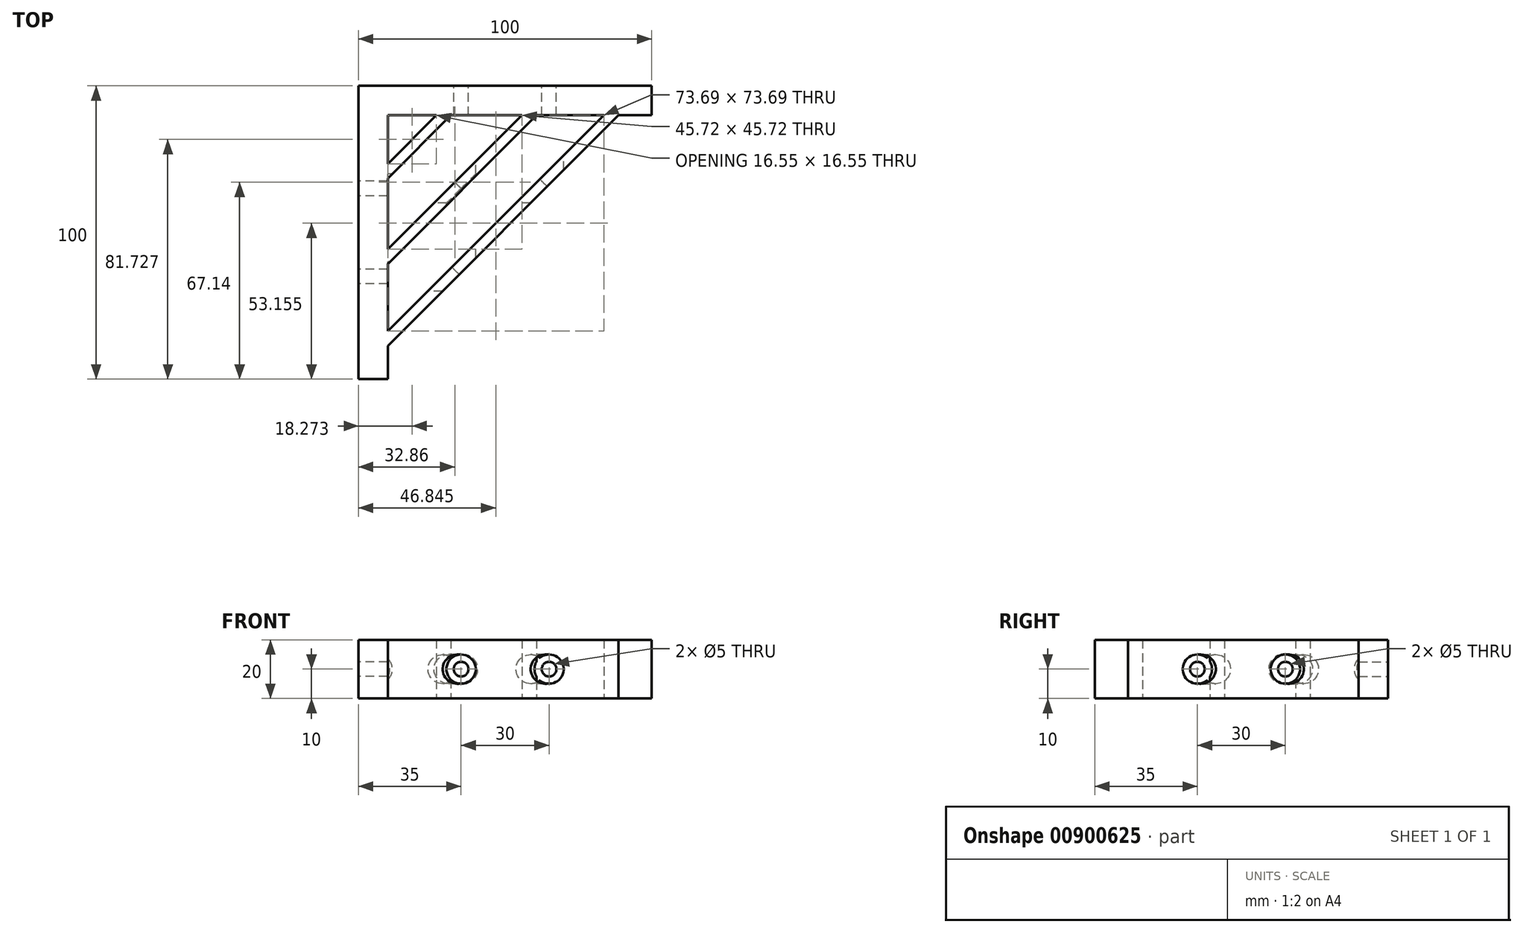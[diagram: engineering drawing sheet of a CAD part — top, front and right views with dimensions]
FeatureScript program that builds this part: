
annotation { "Feature Type Name" : "Feature", "Feature Type Description" : "" }
export const myFeature = defineFeature(function(context is Context, id is Id, definition is map)
    precondition{}
    {
        {
            var Q0;
            Q0=qCreatedBy(makeId("Top.planeOp"),FACE);
            var sketch = newSketch(context, id + "F0", { "sketchPlane" : qUnion([Q0])});
            skLineSegment(sketch, "E0.bottom", {"start": v(-55.72, 55.72) * mm, "end": v(-45.72, 55.72) * mm});
            skLineSegment(sketch, "E0.top", {"start": v(-55.72, -44.28) * mm, "end": v(-45.72, -44.28) * mm});
            skLineSegment(sketch, "E0.left", {"start": v(-55.72, 55.72) * mm, "end": v(-55.72, -44.28) * mm});
            skLineSegment(sketch, "E0.right", {"start": v(-45.72, 55.72) * mm, "end": v(-45.72, -44.28) * mm});
            skLineSegment(sketch, "E1.bottom", {"start": v(-55.72, 55.72) * mm, "end": v(44.28, 55.72) * mm});
            skLineSegment(sketch, "E1.top", {"start": v(-55.72, 45.72) * mm, "end": v(44.28, 45.72) * mm});
            skLineSegment(sketch, "E1.left", {"start": v(-55.72, 55.72) * mm, "end": v(-55.72, 45.72) * mm});
            skLineSegment(sketch, "E1.right", {"start": v(44.28, 55.72) * mm, "end": v(44.28, 45.72) * mm});
            skLineSegment(sketch, "E2", {"start": v(-55.72, 55.72) * mm, "end": v(0, 0) * mm, "construction": true});
            skLineSegment(sketch, "E3", {"start": v(0, 0) * mm, "end": v(47.24, -47.24) * mm, "construction": true});
            skLineSegment(sketch, "E4", {"start": v(-45.72, 29.17) * mm, "end": v(-29.17, 45.72) * mm});
            skLineSegment(sketch, "E5", {"start": v(-29.17, 45.72) * mm, "end": v(-24.17, 45.72) * mm});
            skLineSegment(sketch, "E6", {"start": v(-24.17, 45.72) * mm, "end": v(-45.72, 24.17) * mm});
            skLineSegment(sketch, "E7", {"start": v(-45.72, 0) * mm, "end": v(0, 45.72) * mm});
            skLineSegment(sketch, "E8", {"start": v(0, 45.72) * mm, "end": v(5, 45.72) * mm});
            skLineSegment(sketch, "E9", {"start": v(5, 45.72) * mm, "end": v(-45.72, -5) * mm});
            skLineSegment(sketch, "E10", {"start": v(-45.72, -5) * mm, "end": v(-45.72, 0) * mm});
            skLineSegment(sketch, "E11", {"start": v(-45.72, -27.97) * mm, "end": v(27.97, 45.72) * mm});
            skLineSegment(sketch, "E12", {"start": v(27.97, 45.72) * mm, "end": v(32.97, 45.72) * mm});
            skLineSegment(sketch, "E13", {"start": v(32.97, 45.72) * mm, "end": v(-45.72, -32.97) * mm});
            skLineSegment(sketch, "E14", {"start": v(-45.72, -32.97) * mm, "end": v(-45.72, -27.97) * mm});
            skSolve(sketch);
        }
        {
            var Q0;
            {var subQ6=sQuery(id+"F0.wireOp",EDGE,"E0.top");Q0=makeQuery(id+"F0.imprint","IMPRINT",FACE,{"disambiguationData":[TD([[makeQuery(id+"F0.imprint","IMPRINT",EDGE,{"derivedFrom":subQ6}),1.0]])]});}
            var Q1;
            {var subQ0=sQuery(id+"F0.wireOp",EDGE,"E0.bottom");Q1=makeQuery(id+"F0.imprint","IMPRINT",FACE,{"disambiguationData":[TD([[makeQuery(id+"F0.imprint","IMPRINT",EDGE,{"derivedFrom":subQ0}),-1.0]])]});}
            var Q2;
            {var subQ3=sQuery(id+"F0.wireOp",EDGE,"E1.bottom");Q2=makeQuery(id+"F0.imprint","IMPRINT",FACE,{"disambiguationData":[TD([[makeQuery(id+"F0.imprint","IMPRINT",EDGE,{"derivedFrom":subQ3}),-1.0]])]});}
            var Q3;
            {var subQ2=sQuery(id+"F0.wireOp",EDGE,"E4");Q3=makeQuery(id+"F0.imprint","IMPRINT",FACE,{"disambiguationData":[TD([[makeQuery(id+"F0.imprint","IMPRINT",EDGE,{"derivedFrom":subQ2}),-1.0]])]});}
            var Q4;
            {var subQ0=sQuery(id+"F0.wireOp",EDGE,"E7");Q4=makeQuery(id+"F0.imprint","IMPRINT",FACE,{"disambiguationData":[TD([[makeQuery(id+"F0.imprint","IMPRINT",EDGE,{"derivedFrom":subQ0}),-1.0]])]});}
            var Q5;
            {var subQ0=sQuery(id+"F0.wireOp",EDGE,"E11");Q5=makeQuery(id+"F0.imprint","IMPRINT",FACE,{"disambiguationData":[TD([[makeQuery(id+"F0.imprint","IMPRINT",EDGE,{"derivedFrom":subQ0}),-1.0]])]});}
            extrude(context, id + "F1", {"entities" : qUnion([Q0, Q1, Q2, Q3, Q4, Q5]), "depth" : 20 * mm, "offsetDistance" : 25 * mm});
        }
        {
            var Q0;
            Q0=makeQuery(id+"F1.opExtrude","SWEPT_FACE",FACE,{"disambiguationData":[OSD([sQuery(id+"F0.wireOp",EDGE,"E0.left")])]});
            var sketch = newSketch(context, id + "F2", { "sketchPlane" : qUnion([Q0])});
            skLineSegment(sketch, "E15", {"start": v(-55.72, 10) * mm, "end": v(44.28, 10) * mm, "construction": true});
            skLineSegment(sketch, "E16", {"start": v(-55.72, 10) * mm, "end": v(-20.72, 10) * mm, "construction": true});
            skLineSegment(sketch, "E17", {"start": v(44.28, 10) * mm, "end": v(9.28, 10) * mm, "construction": true});
            skCircle(sketch, "E18", {"center": v(-20.72, 10) * mm, "radius": 2.5 * mm});
            skCircle(sketch, "E19", {"center": v(9.28, 10) * mm, "radius": 2.5 * mm});
            skCircle(sketch, "E20", {"center": v(9.28, 10) * mm, "radius": 5 * mm});
            skCircle(sketch, "E21", {"center": v(-20.72, 10) * mm, "radius": 5 * mm});
            skSolve(sketch);
        }
        {
            var Q0;
            Q0=makeQuery(id+"F2.imprint","IMPRINT",FACE,{"disambiguationData":[TD([[makeQuery(id+"F2.imprint","IMPRINT",EDGE,{"derivedFrom":sQuery(id+"F2.wireOp",EDGE,"E19")}),1.0]])]});
            var Q1;
            Q1=makeQuery(id+"F2.imprint","IMPRINT",FACE,{"disambiguationData":[TD([[makeQuery(id+"F2.imprint","IMPRINT",EDGE,{"derivedFrom":sQuery(id+"F2.wireOp",EDGE,"E19")}),-1.0]])]});
            var Q2;
            Q2=makeQuery(id+"F2.imprint","IMPRINT",FACE,{"disambiguationData":[TD([[makeQuery(id+"F2.imprint","IMPRINT",EDGE,{"derivedFrom":sQuery(id+"F2.wireOp",EDGE,"E18")}),-1.0]])]});
            var Q3;
            Q3=makeQuery(id+"F2.imprint","IMPRINT",FACE,{"disambiguationData":[TD([[makeQuery(id+"F2.imprint","IMPRINT",EDGE,{"derivedFrom":sQuery(id+"F2.wireOp",EDGE,"E18")}),1.0]])]});
            extrude(context, id + "F3", {"entities" : qUnion([Q0, Q1, Q2, Q3]), "operationType" : NewBodyOperationType.REMOVE, "oppositeDirection" : true, "depth" : 86.8 * mm, "offsetDistance" : 25 * mm});
        }
        {
            var Q0;
            Q0=makeQuery(id+"F2.imprint","IMPRINT",FACE,{"disambiguationData":[TD([[makeQuery(id+"F2.imprint","IMPRINT",EDGE,{"derivedFrom":sQuery(id+"F2.wireOp",EDGE,"E18")}),-1.0]])]});
            var Q1;
            Q1=makeQuery(id+"F2.imprint","IMPRINT",FACE,{"disambiguationData":[TD([[makeQuery(id+"F2.imprint","IMPRINT",EDGE,{"derivedFrom":sQuery(id+"F2.wireOp",EDGE,"E19")}),-1.0]])]});
            extrude(context, id + "F4", {"entities" : qUnion([Q0, Q1]), "operationType" : NewBodyOperationType.ADD, "oppositeDirection" : true, "depth" : 10 * mm, "offsetDistance" : 25 * mm});
        }
        {
            var Q0;
            Q0=makeQuery(id+"F1.opExtrude","SWEPT_FACE",FACE,{"disambiguationData":[OSD([sQuery(id+"F0.wireOp",EDGE,"E0.bottom"),sQuery(id+"F0.wireOp",EDGE,"E1.bottom")])]});
            var sketch = newSketch(context, id + "F5", { "sketchPlane" : qUnion([Q0])});
            skLineSegment(sketch, "E22", {"start": v(55.72, 10) * mm, "end": v(20.72, 10) * mm, "construction": true});
            skLineSegment(sketch, "E23", {"start": v(-44.28, 10) * mm, "end": v(-9.28, 10) * mm, "construction": true});
            skCircle(sketch, "E24", {"center": v(20.72, 10) * mm, "radius": 5 * mm});
            skCircle(sketch, "E25", {"center": v(20.72, 10) * mm, "radius": 2.5 * mm});
            skCircle(sketch, "E26", {"center": v(-9.28, 10) * mm, "radius": 5 * mm});
            skCircle(sketch, "E27", {"center": v(-9.28, 10) * mm, "radius": 2.5 * mm});
            skSolve(sketch);
        }
        {
            var Q0;
            Q0=makeQuery(id+"F5.imprint","IMPRINT",FACE,{"disambiguationData":[TD([[makeQuery(id+"F5.imprint","IMPRINT",EDGE,{"derivedFrom":sQuery(id+"F5.wireOp",EDGE,"E25")}),1.0]])]});
            var Q1;
            Q1=makeQuery(id+"F5.imprint","IMPRINT",FACE,{"disambiguationData":[TD([[makeQuery(id+"F5.imprint","IMPRINT",EDGE,{"derivedFrom":sQuery(id+"F5.wireOp",EDGE,"E24")}),1.0]])]});
            var Q2;
            Q2=makeQuery(id+"F5.imprint","IMPRINT",FACE,{"disambiguationData":[TD([[makeQuery(id+"F5.imprint","IMPRINT",EDGE,{"derivedFrom":sQuery(id+"F5.wireOp",EDGE,"E27")}),1.0]])]});
            var Q3;
            Q3=makeQuery(id+"F5.imprint","IMPRINT",FACE,{"disambiguationData":[TD([[makeQuery(id+"F5.imprint","IMPRINT",EDGE,{"derivedFrom":sQuery(id+"F5.wireOp",EDGE,"E26")}),1.0]])]});
            extrude(context, id + "F6", {"entities" : qUnion([Q0, Q1, Q2, Q3]), "operationType" : NewBodyOperationType.REMOVE, "oppositeDirection" : true, "depth" : 102.9 * mm, "offsetDistance" : 25 * mm});
        }
        {
            var Q0;
            Q0=makeQuery(id+"F5.imprint","IMPRINT",FACE,{"disambiguationData":[TD([[makeQuery(id+"F5.imprint","IMPRINT",EDGE,{"derivedFrom":sQuery(id+"F5.wireOp",EDGE,"E26")}),1.0]])]});
            var Q1;
            Q1=makeQuery(id+"F5.imprint","IMPRINT",FACE,{"disambiguationData":[TD([[makeQuery(id+"F5.imprint","IMPRINT",EDGE,{"derivedFrom":sQuery(id+"F5.wireOp",EDGE,"E24")}),1.0]])]});
            extrude(context, id + "F7", {"entities" : qUnion([Q0, Q1]), "operationType" : NewBodyOperationType.ADD, "oppositeDirection" : true, "depth" : 10 * mm, "offsetDistance" : 25 * mm});
        }
    });
